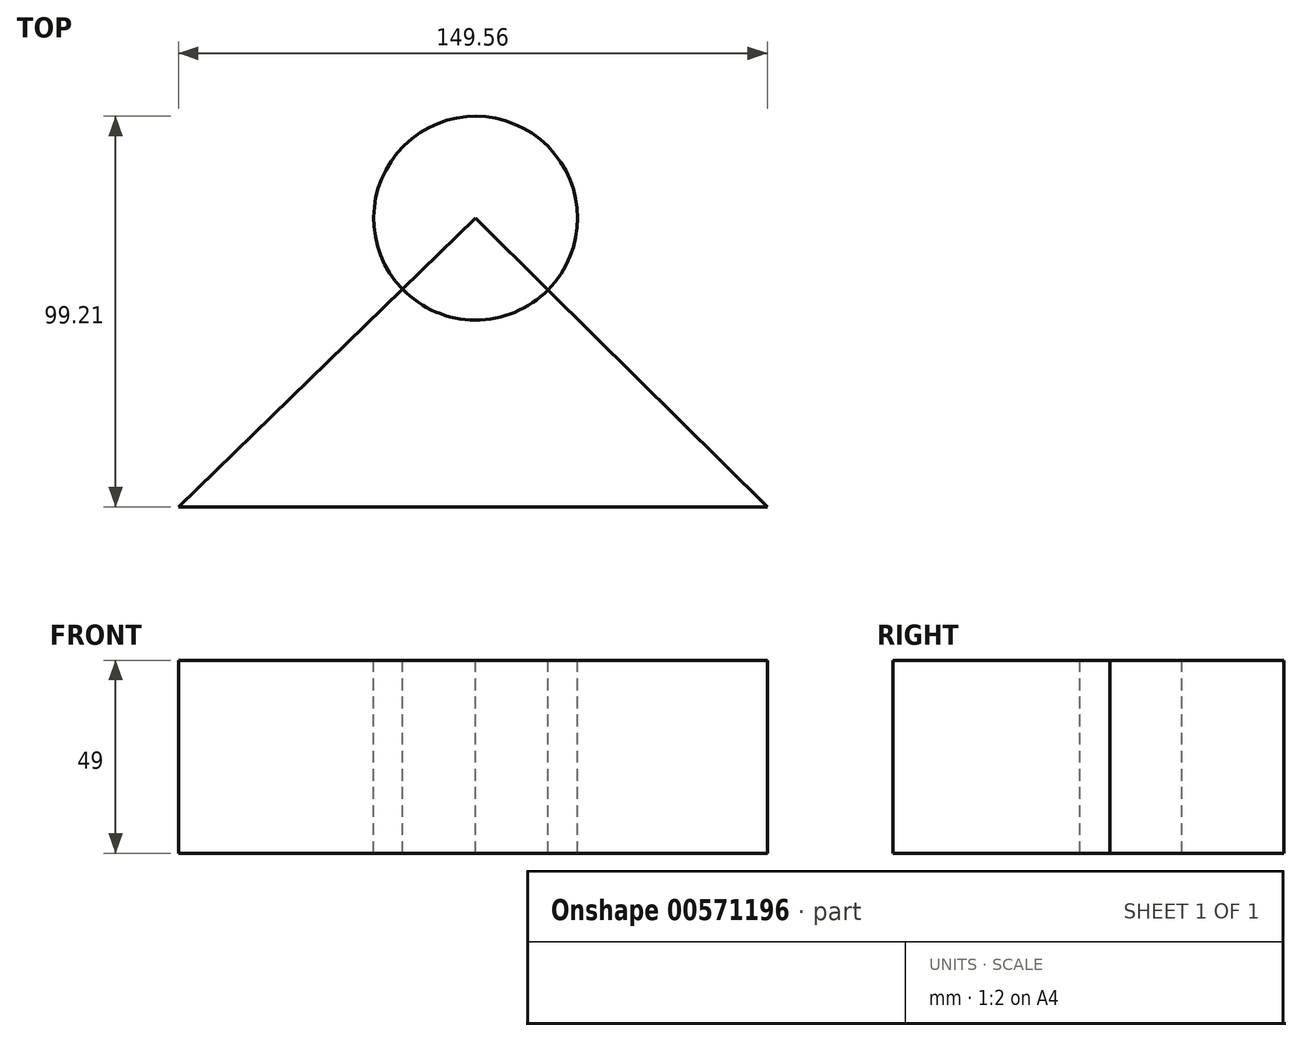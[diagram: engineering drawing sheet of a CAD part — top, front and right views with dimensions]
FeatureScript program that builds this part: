
annotation { "Feature Type Name" : "Feature", "Feature Type Description" : "" }
export const myFeature = defineFeature(function(context is Context, id is Id, definition is map)
    precondition{}
    {
        {
            var Q0;
            Q0=qCreatedBy(makeId("Top.planeOp"),FACE);
            var sketch = newSketch(context, id + "F0", { "sketchPlane" : qUnion([Q0])});
            skLineSegment(sketch, "E0", {"start": v(0, 0) * mm, "end": v(-75.48, -73.33) * mm});
            skLineSegment(sketch, "E1", {"start": v(-75.48, -73.33) * mm, "end": v(74.08, -73.33) * mm});
            skLineSegment(sketch, "E2", {"start": v(74.08, -73.33) * mm, "end": v(0, 0) * mm});
            skCircle(sketch, "E3", {"center": v(0, 0) * mm, "radius": 25.88 * mm});
            skSolve(sketch);
        }
        {
            var Q0;
            {var subQ0=sQuery(id+"F0.wireOp",EDGE,"E1");Q0=makeQuery(id+"F0.imprint","IMPRINT",FACE,{"disambiguationData":[TD([[makeQuery(id+"F0.imprint","IMPRINT",EDGE,{"derivedFrom":subQ0}),1.0]])]});}
            var Q1;
            {var subQ0=sQuery(id+"F0.wireOp",EDGE,"E2");var subQ1=sQuery(id+"F0.wireOp",EDGE,"E0");var subQ2=makeQuery(id+"F0.imprint","INTERSECT",VERTEX,{"derivedFrom":[subQ1,subQ0]});Q1=makeQuery(id+"F0.imprint","IMPRINT",FACE,{"disambiguationData":[TD([[makeQuery(id+"F0.imprint","IMPRINT",EDGE,{"disambiguationData":[TD([[subQ2,-1.0]])],"derivedFrom":subQ1}),-1.0]])]});}
            extrude(context, id + "F1", {"entities" : qUnion([Q0, Q1]), "oppositeDirection" : true, "depth" : 49 * mm, "offsetDistance" : 25 * mm});
        }
    });
